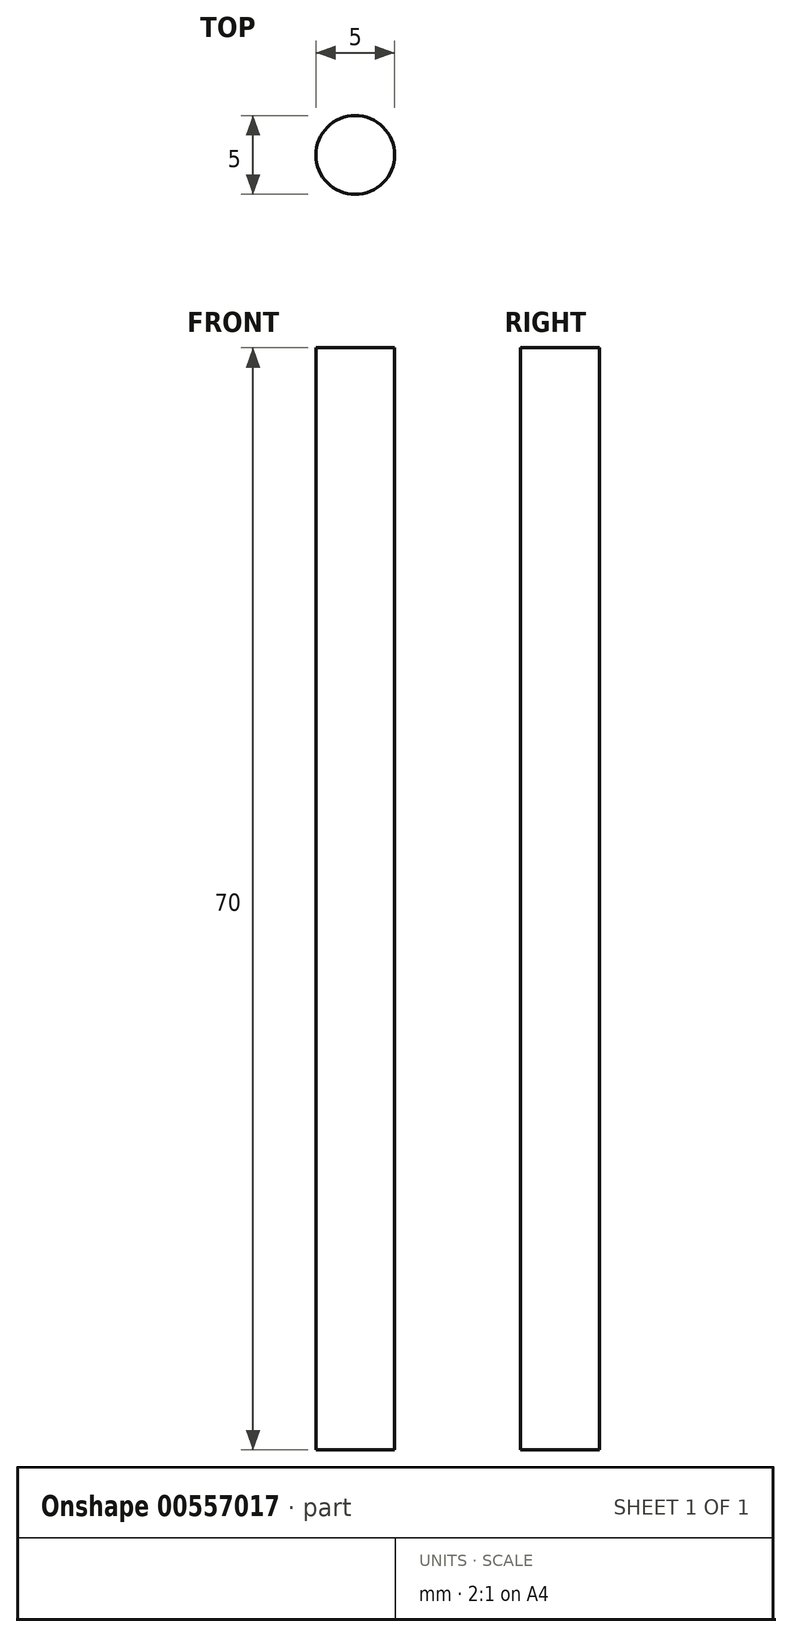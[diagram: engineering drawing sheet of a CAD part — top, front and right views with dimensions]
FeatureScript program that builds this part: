
annotation { "Feature Type Name" : "Feature", "Feature Type Description" : "" }
export const myFeature = defineFeature(function(context is Context, id is Id, definition is map)
    precondition{}
    {
        {
            var Q0;
            Q0=qCreatedBy(makeId("Top.planeOp"),FACE);
            var sketch = newSketch(context, id + "F0", { "sketchPlane" : qUnion([Q0])});
            skCircle(sketch, "E0", {"center": v(0, 0) * mm, "radius": 2.5 * mm});
            skSolve(sketch);
        }
        {
            var Q0;
            Q0=qSketchRegion(id+"F0",true);
            extrude(context, id + "F1", {"entities" : qUnion([Q0]), "depth" : 70 * mm, "offsetDistance" : 25 * mm, "symmetric" : true});
        }
    });
